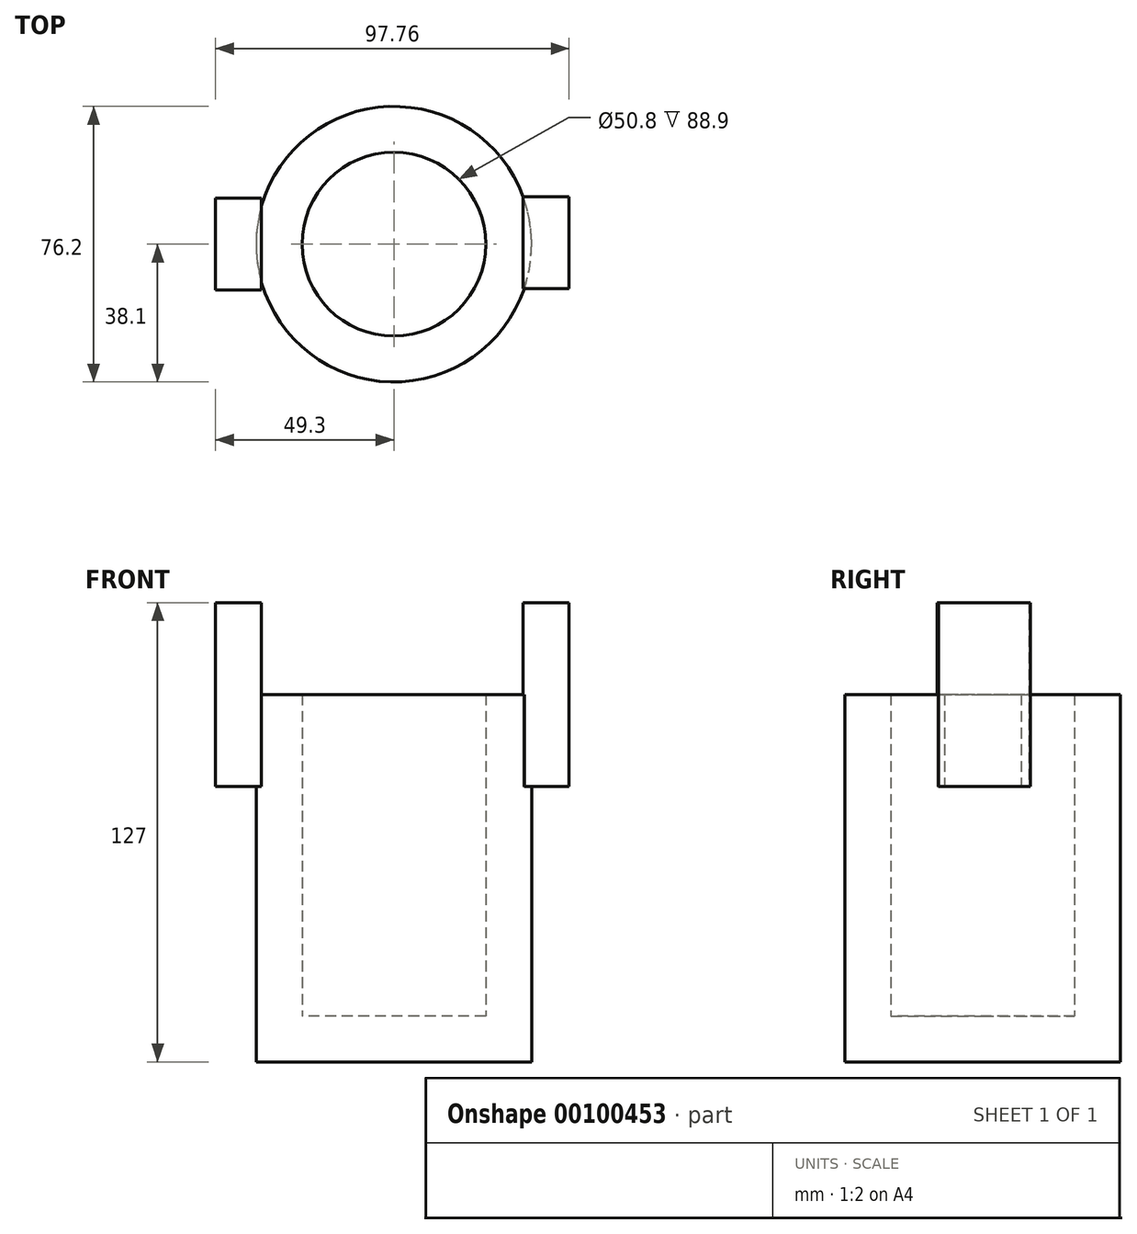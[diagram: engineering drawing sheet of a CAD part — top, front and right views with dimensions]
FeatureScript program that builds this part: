
annotation { "Feature Type Name" : "Feature", "Feature Type Description" : "" }
export const myFeature = defineFeature(function(context is Context, id is Id, definition is map)
    precondition{}
    {
        {
            var Q0;
            Q0=qCreatedBy(makeId("Top.planeOp"),FACE);
            var sketch = newSketch(context, id + "F0", { "sketchPlane" : qUnion([Q0])});
            skCircle(sketch, "E0", {"center": v(0, 0) * mm, "radius": 38.1 * mm});
            skSolve(sketch);
        }
        {
            var Q0;
            Q0 = qSketchRegion(id + "F0", true);
            extrude(context, id + "F1", {"entities" : qUnion([Q0]), "depth" : 101.6 * mm});
        }
        {
            var Q0;
            Q0=makeQuery(id+"F1.opExtrude","CAP_FACE",FACE,{"disambiguationData":[OSD([sQuery(id+"F0.wireOp",EDGE,"E0")])],"isStart":false});
            var sketch = newSketch(context, id + "F2", { "sketchPlane" : qUnion([Q0])});
            skLineSegment(sketch, "E1.bottom", {"start": v(-49.3, -12.65) * mm, "end": v(-36.6, -12.65) * mm});
            skLineSegment(sketch, "E1.top", {"start": v(-49.3, 12.75) * mm, "end": v(-36.6, 12.75) * mm});
            skLineSegment(sketch, "E1.left", {"start": v(-49.3, -12.65) * mm, "end": v(-49.3, 12.75) * mm});
            skLineSegment(sketch, "E1.right", {"start": v(-36.6, -12.65) * mm, "end": v(-36.6, 12.75) * mm});
            skLineSegment(sketch, "E2.bottom", {"start": v(35.76, 13.15) * mm, "end": v(48.46, 13.15) * mm});
            skLineSegment(sketch, "E2.top", {"start": v(35.76, -12.25) * mm, "end": v(48.46, -12.25) * mm});
            skLineSegment(sketch, "E2.left", {"start": v(35.76, 13.15) * mm, "end": v(35.76, -12.25) * mm});
            skLineSegment(sketch, "E2.right", {"start": v(48.46, 13.15) * mm, "end": v(48.46, -12.25) * mm});
            skLineSegment(sketch, "E3.bottom", {"start": v(39.96, 23.8) * mm, "end": v(39.96, 23.8) * mm});
            skLineSegment(sketch, "E3.top", {"start": v(39.96, 22.23) * mm, "end": v(39.96, 22.23) * mm});
            skLineSegment(sketch, "E3.left", {"start": v(39.96, 23.8) * mm, "end": v(39.96, 22.23) * mm});
            skLineSegment(sketch, "E3.right", {"start": v(39.96, 23.8) * mm, "end": v(39.96, 22.23) * mm});
            skSolve(sketch);
        }
        {
            var Q0;
            Q0 = qSketchRegion(id + "F2", true);
            extrude(context, id + "F3", {"entities" : qUnion([Q0]), "operationType" : NewBodyOperationType.ADD, "endBound" : BoundingType.SYMMETRIC, "depth" : 50.8 * mm});
        }
        {
            var Q0;
            Q0=makeQuery(id+"F1.opExtrude","CAP_FACE",FACE,{"disambiguationData":[OSD([sQuery(id+"F0.wireOp",EDGE,"E0")])],"isStart":false});
            shell(context, id + "F4", {"entities" : qUnion([Q0]), "thickness" : 12.7 * mm});
        }
    });
